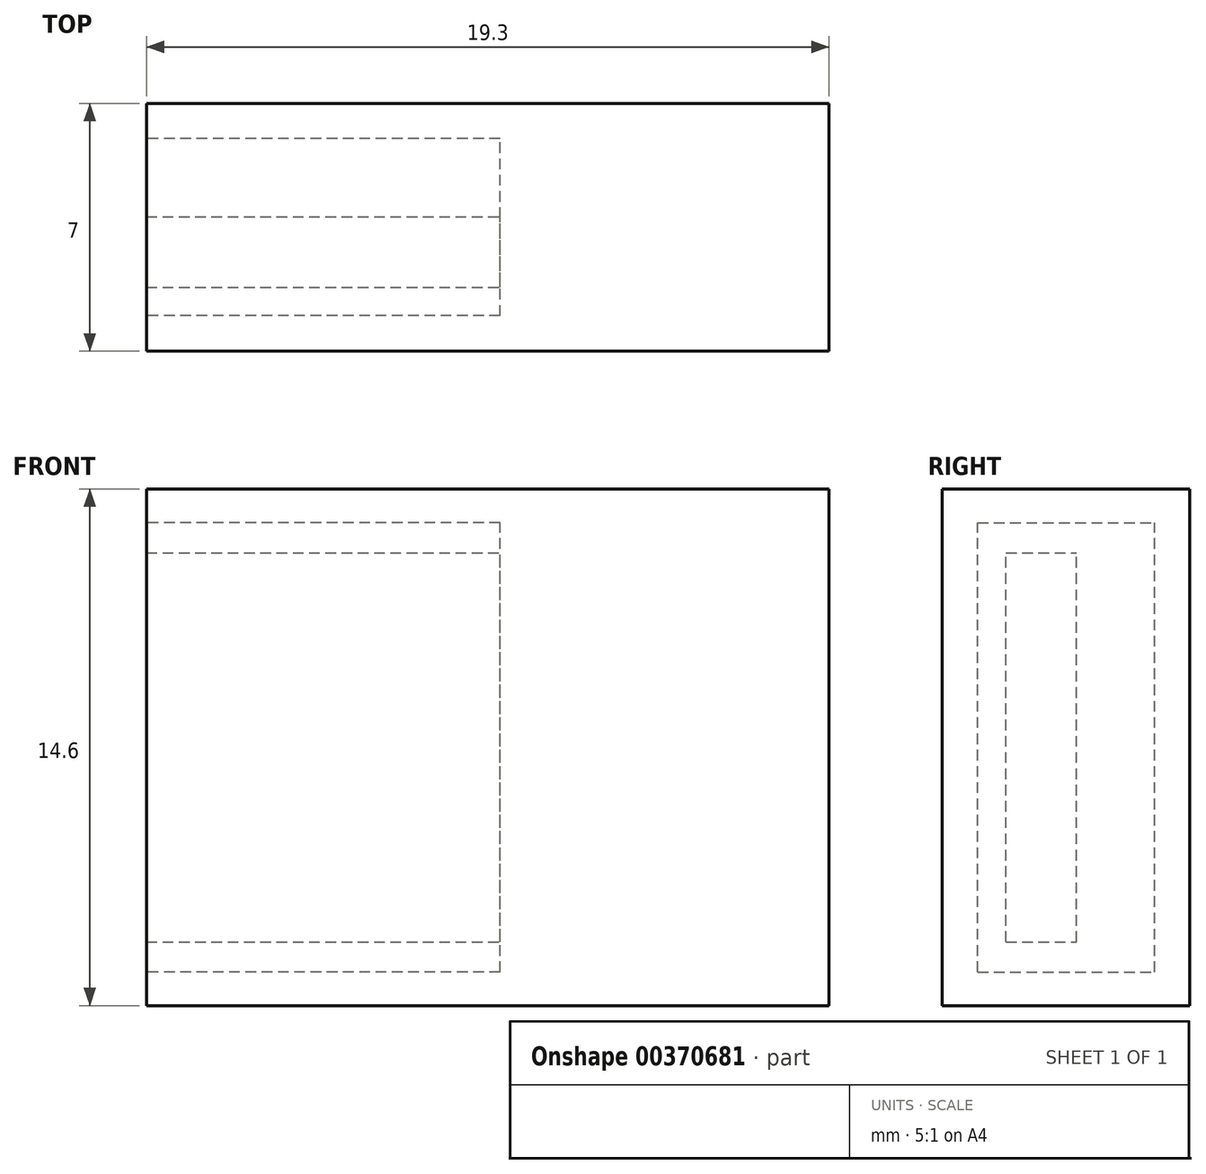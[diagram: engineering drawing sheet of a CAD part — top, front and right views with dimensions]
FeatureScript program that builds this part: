
annotation { "Feature Type Name" : "Feature", "Feature Type Description" : "" }
export const myFeature = defineFeature(function(context is Context, id is Id, definition is map)
    precondition{}
    {
        {
            var Q0;
            Q0=qCreatedBy(makeId("Front.planeOp"),FACE);
            var sketch = newSketch(context, id + "F0", { "sketchPlane" : qUnion([Q0])});
            skLineSegment(sketch, "E0.bottom", {"start": v(0, 0) * mm, "end": v(19.3, 0) * mm});
            skLineSegment(sketch, "E0.top", {"start": v(0, 14.6) * mm, "end": v(19.3, 14.6) * mm});
            skLineSegment(sketch, "E0.left", {"start": v(0, 0) * mm, "end": v(0, 14.6) * mm});
            skLineSegment(sketch, "E0.right", {"start": v(19.3, 0) * mm, "end": v(19.3, 14.6) * mm});
            skSolve(sketch);
        }
        {
            var Q0;
            Q0 = qSketchRegion(id + "F0", true);
            extrude(context, id + "F1", {"entities" : qUnion([Q0]), "depth" : 7 * mm});
        }
        {
            var Q0;
            Q0=makeQuery(id+"F1.opExtrude","SWEPT_FACE",FACE,{"disambiguationData":[OSD([sQuery(id+"F0.wireOp",EDGE,"E0.left")])]});
            var sketch = newSketch(context, id + "F2", { "sketchPlane" : qUnion([Q0])});
            skLineSegment(sketch, "E1.bottom", {"start": v(6, 0.95) * mm, "end": v(1, 0.95) * mm});
            skLineSegment(sketch, "E1.top", {"start": v(6, 13.65) * mm, "end": v(1, 13.65) * mm});
            skLineSegment(sketch, "E1.left", {"start": v(6, 0.95) * mm, "end": v(6, 13.65) * mm});
            skLineSegment(sketch, "E1.right", {"start": v(1, 0.95) * mm, "end": v(1, 13.65) * mm});
            skPoint(sketch, "E1.middle", {"position": v(3.5, 7.3) * mm});
            skPoint(sketch, "E1.middle.positionSnap0", {"position": v(3.5, 14.6) * mm});
            skPoint(sketch, "E1.middle.positionSnap1", {"position": v(0, 7.3) * mm});
            skPoint(sketch, "E1.centerSnap0", {"position": v(3.5, 14.6) * mm});
            skPoint(sketch, "E1.centerSnap1", {"position": v(0, 7.3) * mm});
            skSolve(sketch);
        }
        {
            var Q0;
            Q0 = qSketchRegion(id + "F2", true);
            extrude(context, id + "F3", {"entities" : qUnion([Q0]), "operationType" : NewBodyOperationType.REMOVE, "oppositeDirection" : true, "depth" : 10 * mm});
        }
        {
            var Q0;
            Q0=makeQuery(id+"F3.boolean.opBoolean","COPY",FACE,{"derivedFrom":makeQuery(id+"F3.opExtrude","CAP_FACE",FACE,{"disambiguationData":[OSD([sQuery(id+"F2.wireOp",EDGE,"E1.bottom"),sQuery(id+"F2.wireOp",EDGE,"E1.top"),sQuery(id+"F2.wireOp",EDGE,"E1.left"),sQuery(id+"F2.wireOp",EDGE,"E1.right")])],"isStart":false})});
            var sketch = newSketch(context, id + "F4", { "sketchPlane" : qUnion([Q0])});
            skLineSegment(sketch, "E2.bottom", {"start": v(5.2, 1.8) * mm, "end": v(3.2, 1.8) * mm});
            skLineSegment(sketch, "E2.top", {"start": v(5.2, 12.8) * mm, "end": v(3.2, 12.8) * mm});
            skLineSegment(sketch, "E2.left", {"start": v(5.2, 1.8) * mm, "end": v(5.2, 12.8) * mm});
            skLineSegment(sketch, "E2.right", {"start": v(3.2, 1.8) * mm, "end": v(3.2, 12.8) * mm});
            skPoint(sketch, "E2.middle", {"position": v(4.2, 7.3) * mm});
            skPoint(sketch, "E2.middle.positionSnap0", {"position": v(6, 7.3) * mm});
            skPoint(sketch, "E2.centerSnap0", {"position": v(6, 7.3) * mm});
            skSolve(sketch);
        }
        {
            var Q0;
            Q0 = qSketchRegion(id + "F4", true);
            extrude(context, id + "F5", {"entities" : qUnion([Q0]), "operationType" : NewBodyOperationType.ADD, "depth" : 10 * mm});
        }
    });
